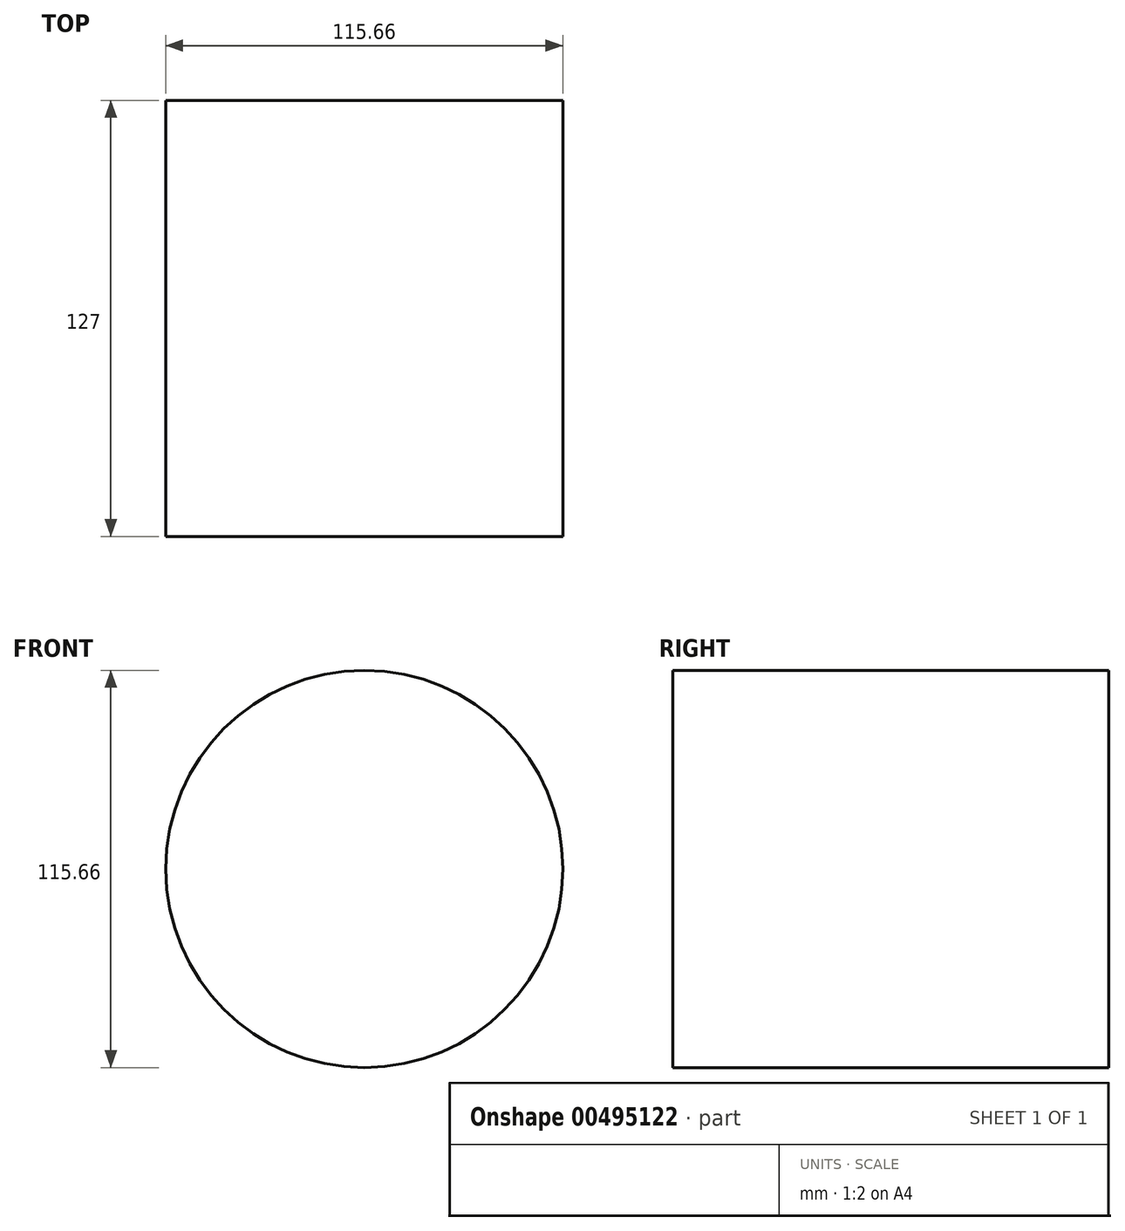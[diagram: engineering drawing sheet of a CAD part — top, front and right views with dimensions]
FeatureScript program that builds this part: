
annotation { "Feature Type Name" : "Feature", "Feature Type Description" : "" }
export const myFeature = defineFeature(function(context is Context, id is Id, definition is map)
    precondition{}
    {
        {
            var Q0;
            Q0=qCreatedBy(makeId("Front.planeOp"),FACE);
            var sketch = newSketch(context, id + "F0", { "sketchPlane" : qUnion([Q0])});
            skCircle(sketch, "E0", {"center": v(0, 0) * mm, "radius": 57.83 * mm});
            skSolve(sketch);
        }
        {
            var Q0;
            Q0=makeQuery(id+"F0.imprint","IMPRINT",FACE,{"disambiguationData":[TD([[makeQuery(id+"F0.imprint","IMPRINT",EDGE,{"derivedFrom":sQuery(id+"F0.wireOp",EDGE,"E0")}),1.0]])]});
            var Q1;
            Q1 = qSketchRegion(id + "F0", true);
            extrude(context, id + "F1", {"entities" : qUnion([Q0, Q1]), "depth" : 127 * mm});
        }
    });
